# Revit family: Unterlegscheibe DIN440 9 A2
name_source: partatom
category: Generic Models
revit_build: Autodesk Revit 2017 (Build: 20190508_0315(x64)
units: mm (PartAtom-declared; Revit-internal decimal feet)

## family parameters
Always vertical = Yes
Can host rebar = No
Cut with Voids When Loaded = No
Part Type = Normal
Room Calculation Point = No
Round Connector Dimension = Use Diameter
Shared = No
Work Plane-Based = No

## types (1)
- DIN440 9 A2
    Article Type = DIN440 9 A2
    Diameter = 28 mm  [stored 0.0918635 ft]
    Diameter 1 = 9 mm  [stored 0.0295276 ft]
    GTIN = 4012196712205
    Height = 3 mm  [stored 0.00984252 ft]
    Manufacturer = OBO BETTERMANN
    Manufacturer Art.No. = 6408715
    Material = Edelstahl, rostfrei 1.4301
    URL = http://www.obo-bettermann.com

note: [stored X ft] marks values corroborated as IEEE doubles in the binary element streams (Revit-internal decimal feet)

## geometry (parser evidence)
native form markers: Sweep x3
no freeform markers — native parametric forms only
